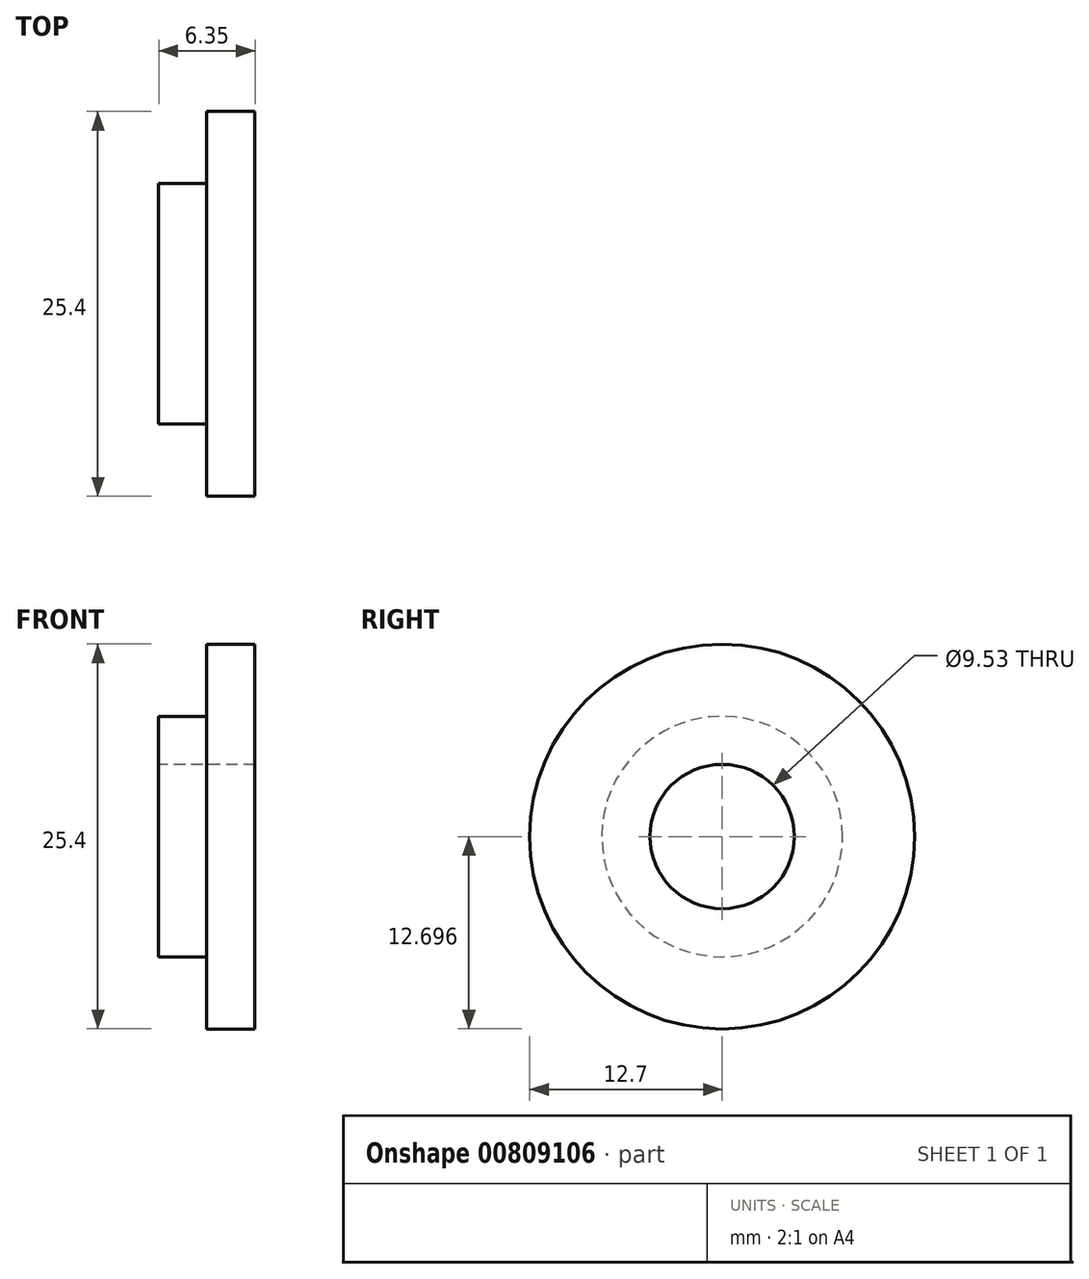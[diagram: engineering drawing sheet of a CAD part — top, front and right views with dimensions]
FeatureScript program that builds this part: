
annotation { "Feature Type Name" : "Feature", "Feature Type Description" : "" }
export const myFeature = defineFeature(function(context is Context, id is Id, definition is map)
    precondition{}
    {
        {
            var Q0;
            Q0=qCreatedBy(makeId("Front.planeOp"),FACE);
            var sketch = newSketch(context, id + "F0", { "sketchPlane" : qUnion([Q0])});
            skLineSegment(sketch, "E0", {"start": v(-23.9, -6.68) * mm, "end": v(86.98, -6.68) * mm});
            skLineSegment(sketch, "E1.bottom", {"start": v(-1.68, -1.92) * mm, "end": v(-8.03, -1.92) * mm});
            skLineSegment(sketch, "E1.top", {"start": v(-1.68, 6.02) * mm, "end": v(-8.03, 6.02) * mm});
            skLineSegment(sketch, "E1.left", {"start": v(-1.68, -1.92) * mm, "end": v(-1.68, 6.02) * mm});
            skLineSegment(sketch, "E1.right", {"start": v(-8.03, -1.92) * mm, "end": v(-8.03, 6.02) * mm});
            skLineSegment(sketch, "E2.bottom", {"start": v(-8.03, 6.02) * mm, "end": v(-4.86, 6.02) * mm});
            skLineSegment(sketch, "E2.top", {"start": v(-8.03, 1.25) * mm, "end": v(-4.86, 1.25) * mm});
            skLineSegment(sketch, "E2.left", {"start": v(-8.03, 6.02) * mm, "end": v(-8.03, 1.25) * mm});
            skLineSegment(sketch, "E2.right", {"start": v(-4.86, 6.02) * mm, "end": v(-4.86, 1.25) * mm});
            skCircle(sketch, "E3", {"center": v(-27.08, 2.84) * mm, "radius": 0.8 * mm});
            skSolve(sketch);
        }
        {
            var Q0;
            Q0=makeQuery(id+"F0.imprint","IMPRINT",FACE,{"disambiguationData":[TD([[makeQuery(id+"F0.imprint","IMPRINT",EDGE,{"derivedFrom":sQuery(id+"F0.wireOp",EDGE,"E1.bottom")}),-1.0]])]});
            var Q1;
            Q1=sQuery(id+"F0.wireOp",EDGE,"E0");
            revolve(context, id + "F1", {"surfaceOperationType" : NewSurfaceOperationType.NEW, "entities" : qUnion([Q0]), "axis" : qUnion([Q1]), "revolveType" : RevolveType.FULL});
        }
    });
